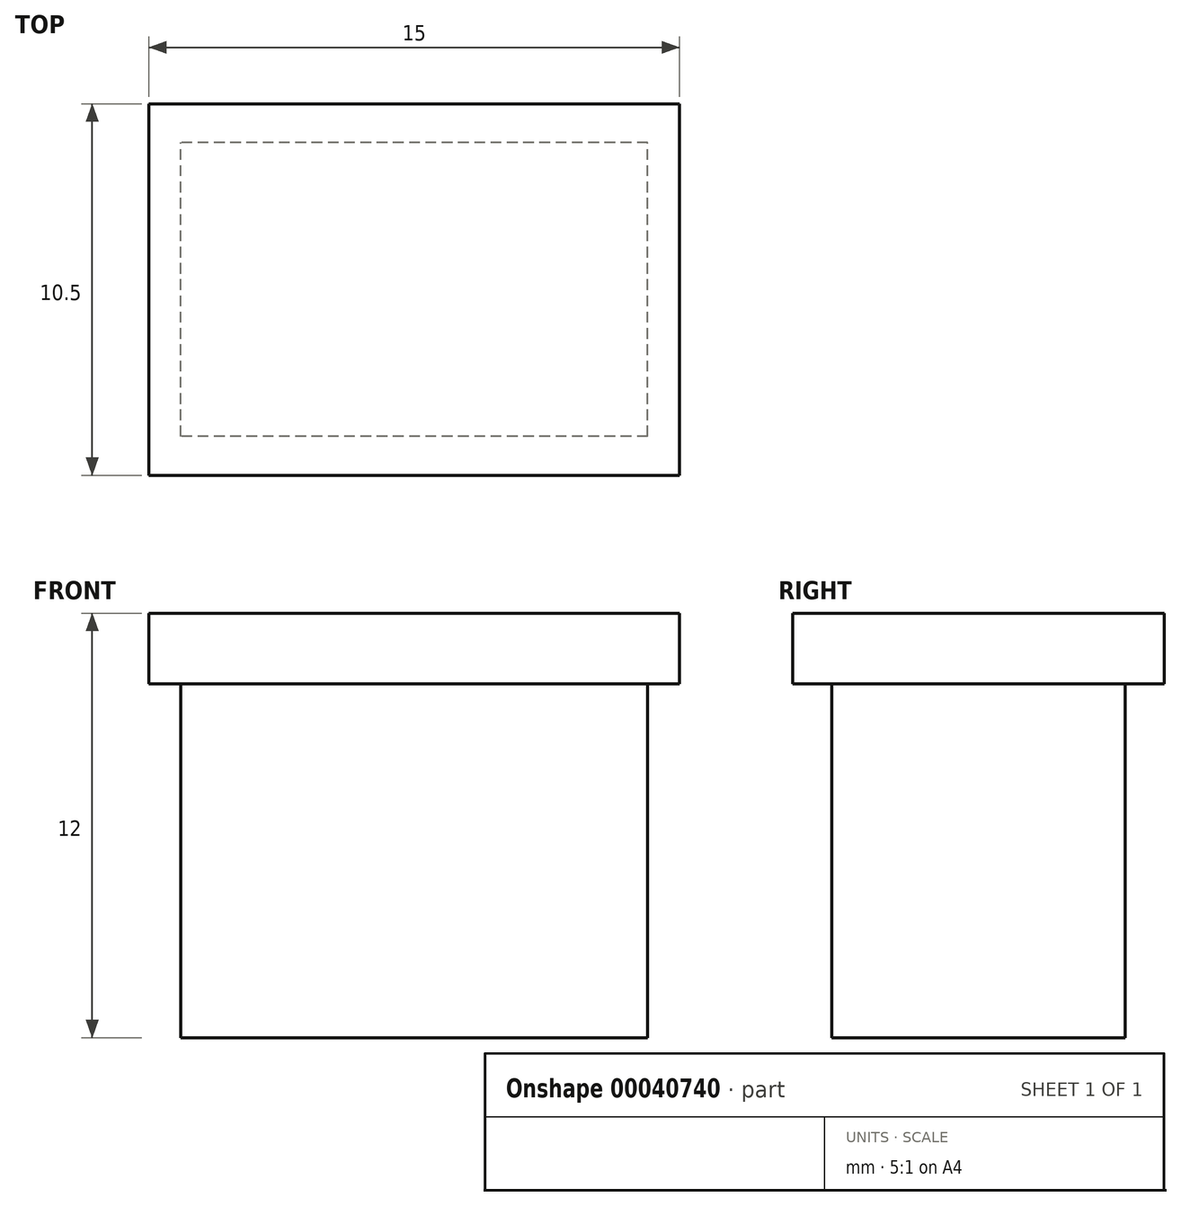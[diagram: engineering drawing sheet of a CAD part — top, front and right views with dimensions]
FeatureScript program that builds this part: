
annotation { "Feature Type Name" : "Feature", "Feature Type Description" : "" }
export const myFeature = defineFeature(function(context is Context, id is Id, definition is map)
    precondition{}
    {
        {
            var Q0;
            Q0=qCreatedBy(makeId("Top.planeOp"),FACE);
            var sketch = newSketch(context, id + "F0", { "sketchPlane" : qUnion([Q0])});
            skLineSegment(sketch, "E0.rect.bottom", {"start": v(6.6, -4.15) * mm, "end": v(-6.6, -4.15) * mm});
            skLineSegment(sketch, "E0.rect.top", {"start": v(6.6, 4.15) * mm, "end": v(-6.6, 4.15) * mm});
            skLineSegment(sketch, "E0.rect.left", {"start": v(6.6, -4.15) * mm, "end": v(6.6, 4.15) * mm});
            skLineSegment(sketch, "E0.rect.right", {"start": v(-6.6, -4.15) * mm, "end": v(-6.6, 4.15) * mm});
            skPoint(sketch, "E0.rect.middle", {"position": v(0, 0) * mm});
            skSolve(sketch);
        }
        {
            var Q0;
            Q0=makeQuery(id+"F0.imprint","IMPRINT",FACE,{"disambiguationData":[TD([[makeQuery(id+"F0.imprint","IMPRINT",EDGE,{"derivedFrom":sQuery(id+"F0.wireOp",EDGE,"E0.rect.bottom")}),-1.0]])]});
            extrude(context, id + "F1", {"entities" : qUnion([Q0]), "depth" : 10 * mm});
        }
        {
            var Q0;
            Q0=makeQuery(id+"F1.opExtrude","CAP_FACE",FACE,{"disambiguationData":[OSD([sQuery(id+"F0.wireOp",EDGE,"E0.rect.bottom"),sQuery(id+"F0.wireOp",EDGE,"E0.rect.top"),sQuery(id+"F0.wireOp",EDGE,"E0.rect.left"),sQuery(id+"F0.wireOp",EDGE,"E0.rect.right")])],"isStart":false});
            var sketch = newSketch(context, id + "F2", { "sketchPlane" : qUnion([Q0])});
            skLineSegment(sketch, "E1.rect.bottom", {"start": v(7.5, -5.25) * mm, "end": v(-7.5, -5.25) * mm});
            skLineSegment(sketch, "E1.rect.top", {"start": v(7.5, 5.25) * mm, "end": v(-7.5, 5.25) * mm});
            skLineSegment(sketch, "E1.rect.left", {"start": v(7.5, -5.25) * mm, "end": v(7.5, 5.25) * mm});
            skLineSegment(sketch, "E1.rect.right", {"start": v(-7.5, -5.25) * mm, "end": v(-7.5, 5.25) * mm});
            skPoint(sketch, "E1.rect.middle", {"position": v(0, 0) * mm});
            skSolve(sketch);
        }
        {
            var Q0;
            Q0=makeQuery(id+"F2.imprint","IMPRINT",FACE,{"disambiguationData":[TD([[makeQuery(id+"F2.imprint","IMPRINT",EDGE,{"derivedFrom":sQuery(id+"F2.wireOp",EDGE,"E1.rect.bottom")}),-1.0]])]});
            var Q1;
            Q1=makeQuery(id+"F2.imprint","IMPRINT",FACE,{"disambiguationData":[TD([[makeQuery(id+"F2.imprint","IMPRINT",EDGE,{"derivedFrom":makeQuery(id+"F1.opExtrude","CAP_EDGE",EDGE,{"disambiguationData":[OSD([sQuery(id+"F0.wireOp",EDGE,"E0.rect.bottom")])],"isStart":false})}),-1.0]])]});
            extrude(context, id + "F3", {"entities" : qUnion([Q0, Q1]), "operationType" : NewBodyOperationType.ADD, "depth" : 2 * mm});
        }
    });
